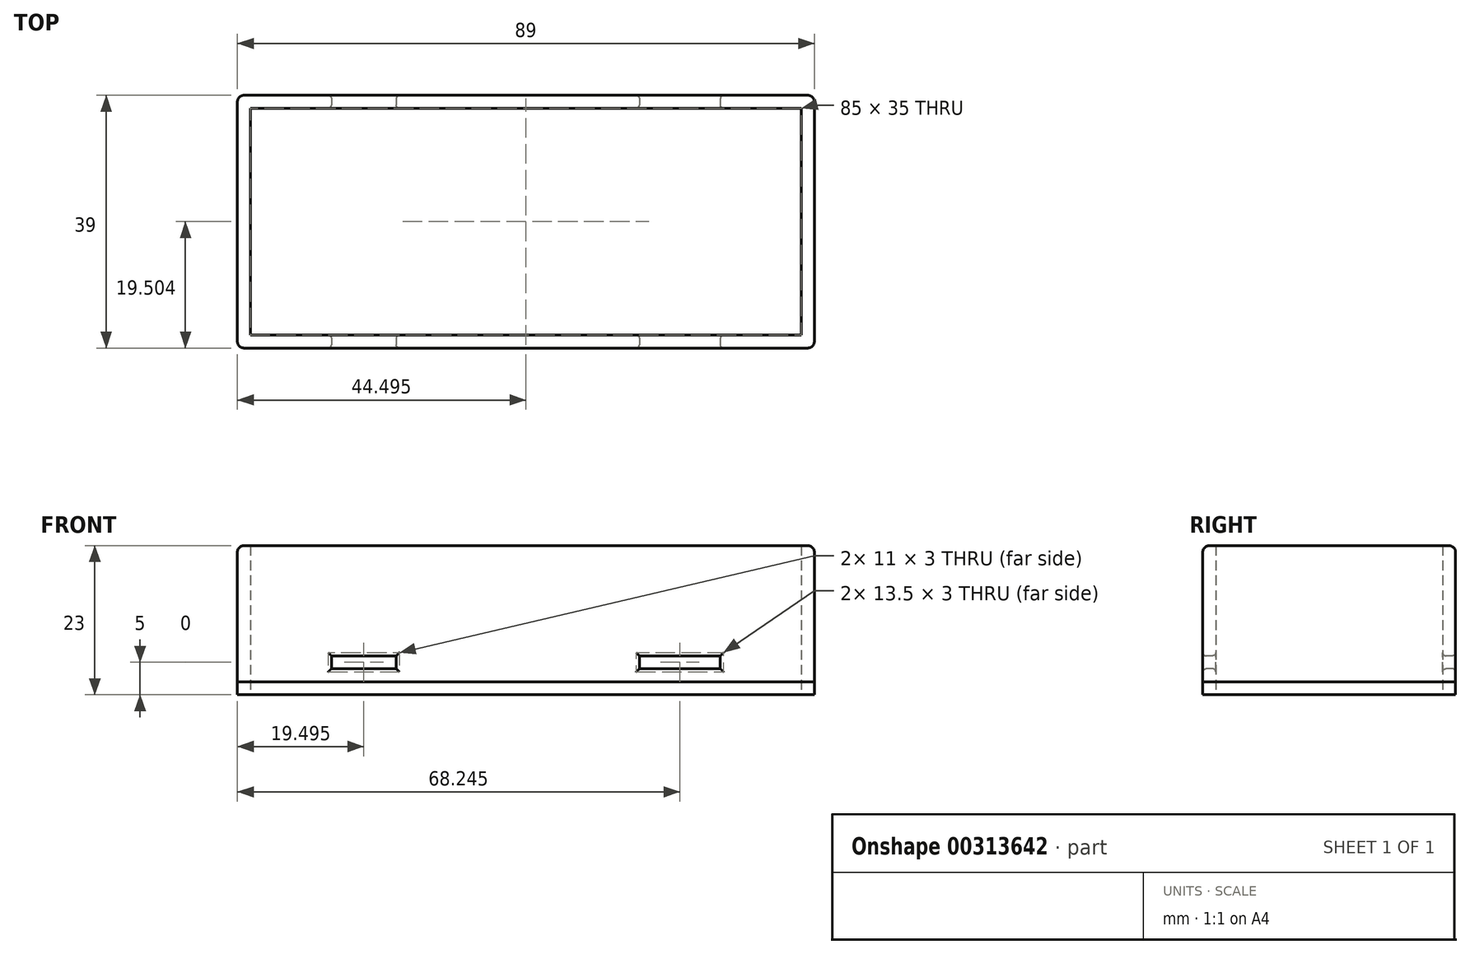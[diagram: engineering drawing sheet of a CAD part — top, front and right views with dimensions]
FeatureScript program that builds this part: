
annotation { "Feature Type Name" : "Feature", "Feature Type Description" : "" }
export const myFeature = defineFeature(function(context is Context, id is Id, definition is map)
    precondition{}
    {
        {
            var Q0;
            Q0=qCreatedBy(makeId("Top.planeOp"),FACE);
            var sketch = newSketch(context, id + "F0", { "sketchPlane" : qUnion([Q0])});
            skLineSegment(sketch, "E0.bottom", {"start": v(-28.21, 17.15) * mm, "end": v(60.79, 17.15) * mm});
            skLineSegment(sketch, "E0.top", {"start": v(-28.21, -21.85) * mm, "end": v(60.79, -21.85) * mm});
            skLineSegment(sketch, "E0.left", {"start": v(-28.21, 17.15) * mm, "end": v(-28.21, -21.85) * mm});
            skLineSegment(sketch, "E0.right", {"start": v(60.79, 17.15) * mm, "end": v(60.79, -21.85) * mm});
            skLineSegment(sketch, "E1.bottom", {"start": v(-26.21, 15.15) * mm, "end": v(58.79, 15.15) * mm});
            skLineSegment(sketch, "E1.top", {"start": v(-26.21, -19.85) * mm, "end": v(58.79, -19.85) * mm});
            skLineSegment(sketch, "E1.left", {"start": v(-26.21, 15.15) * mm, "end": v(-26.21, -19.85) * mm});
            skLineSegment(sketch, "E1.right", {"start": v(58.79, 15.15) * mm, "end": v(58.79, -19.85) * mm});
            skSolve(sketch);
        }
        {
            var Q0;
            Q0=makeQuery(id+"F0.imprint","IMPRINT",FACE,{"disambiguationData":[TD([[makeQuery(id+"F0.imprint","IMPRINT",EDGE,{"derivedFrom":sQuery(id+"F0.wireOp",EDGE,"E0.bottom")}),-1.0]])]});
            extrude(context, id + "F1", {"entities" : qUnion([Q0]), "depth" : 23 * mm});
        }
        {
            var Q0;
            Q0=qCreatedBy(makeId("Top.planeOp"),FACE);
            var sketch = newSketch(context, id + "F2", { "sketchPlane" : qUnion([Q0])});
            skLineSegment(sketch, "E2.bottom", {"start": v(-28.21, -21.85) * mm, "end": v(60.79, -21.85) * mm});
            skLineSegment(sketch, "E2.top", {"start": v(-28.21, 17.15) * mm, "end": v(60.79, 17.15) * mm});
            skLineSegment(sketch, "E2.left", {"start": v(-28.21, -21.85) * mm, "end": v(-28.21, 17.15) * mm});
            skLineSegment(sketch, "E2.right", {"start": v(60.79, -21.85) * mm, "end": v(60.79, 17.15) * mm});
            skSolve(sketch);
        }
        {
            var Q0;
            Q0 = qSketchRegion(id + "F2", true);
            extrude(context, id + "F3", {"entities" : qUnion([Q0]), "depth" : 2 * mm});
        }
        {
            var Q0;
            Q0=makeQuery(id+"F1.opExtrude","CAP_EDGE",EDGE,{"disambiguationData":[OSD([sQuery(id+"F0.wireOp",EDGE,"E0.bottom")])],"isStart":false});
            var Q1;
            Q1=makeQuery(id+"F1.opExtrude","CAP_EDGE",EDGE,{"disambiguationData":[OSD([sQuery(id+"F0.wireOp",EDGE,"E0.left")])],"isStart":false});
            var Q2;
            Q2=makeQuery(id+"F1.opExtrude","CAP_EDGE",EDGE,{"disambiguationData":[OSD([sQuery(id+"F0.wireOp",EDGE,"E0.top")])],"isStart":false});
            var Q3;
            Q3=makeQuery(id+"F1.opExtrude","CAP_EDGE",EDGE,{"disambiguationData":[OSD([sQuery(id+"F0.wireOp",EDGE,"E0.right")])],"isStart":false});
            var Q4;
            Q4=makeQuery(id+"F1.opExtrude","SWEPT_EDGE",EDGE,{"disambiguationData":[OSD([sQuery(id+"F0.wireOp",EDGE,"E0.bottom"),sQuery(id+"F0.wireOp",EDGE,"E0.right")])]});
            var Q5;
            Q5=makeQuery(id+"F1.opExtrude","SWEPT_EDGE",EDGE,{"disambiguationData":[OSD([sQuery(id+"F0.wireOp",EDGE,"E0.top"),sQuery(id+"F0.wireOp",EDGE,"E0.right")])]});
            var Q6;
            Q6=makeQuery(id+"F1.opExtrude","SWEPT_EDGE",EDGE,{"disambiguationData":[OSD([sQuery(id+"F0.wireOp",EDGE,"E0.bottom"),sQuery(id+"F0.wireOp",EDGE,"E0.left")])]});
            var Q7;
            Q7=makeQuery(id+"F1.opExtrude","SWEPT_EDGE",EDGE,{"disambiguationData":[OSD([sQuery(id+"F0.wireOp",EDGE,"E0.top"),sQuery(id+"F0.wireOp",EDGE,"E0.left")])]});
            fillet(context, id + "F4", {"entities" : qUnion([Q0, Q1, Q2, Q3, Q4, Q5, Q6, Q7]), "radius" : 1 * mm, "tangentPropagation" : true, "allowEdgeOverflow" : false});
        }
        {
            var Q0;
            Q0=makeQuery(id+"F3.opExtrude","SWEPT_EDGE",EDGE,{"disambiguationData":[OSD([sQuery(id+"F2.wireOp",EDGE,"E2.top"),sQuery(id+"F2.wireOp",EDGE,"E2.right")])]});
            var Q1;
            Q1=makeQuery(id+"F3.opExtrude","SWEPT_EDGE",EDGE,{"disambiguationData":[OSD([sQuery(id+"F2.wireOp",EDGE,"E2.top"),sQuery(id+"F2.wireOp",EDGE,"E2.left")])]});
            var Q2;
            Q2=makeQuery(id+"F3.opExtrude","SWEPT_EDGE",EDGE,{"disambiguationData":[OSD([sQuery(id+"F2.wireOp",EDGE,"E2.bottom"),sQuery(id+"F2.wireOp",EDGE,"E2.left")])]});
            var Q3;
            Q3=makeQuery(id+"F3.opExtrude","SWEPT_EDGE",EDGE,{"disambiguationData":[OSD([sQuery(id+"F2.wireOp",EDGE,"E2.bottom"),sQuery(id+"F2.wireOp",EDGE,"E2.right")])]});
            fillet(context, id + "F5", {"entities" : qUnion([Q0, Q1, Q2, Q3]), "radius" : 1 * mm, "tangentPropagation" : true, "allowEdgeOverflow" : false});
        }
        {
            var Q0;
            Q0=qCreatedBy(makeId("Front.planeOp"),FACE);
            var sketch = newSketch(context, id + "F6", { "sketchPlane" : qUnion([Q0])});
            skLineSegment(sketch, "E3.bottom", {"start": v(-13.71, 6) * mm, "end": v(-3.71, 6) * mm});
            skLineSegment(sketch, "E3.top", {"start": v(-13.71, 4) * mm, "end": v(-3.71, 4) * mm});
            skLineSegment(sketch, "E3.left", {"start": v(-13.71, 6) * mm, "end": v(-13.71, 4) * mm});
            skLineSegment(sketch, "E3.right", {"start": v(-3.71, 6) * mm, "end": v(-3.71, 4) * mm});
            skLineSegment(sketch, "E4.bottom", {"start": v(33.79, 6) * mm, "end": v(46.29, 6) * mm});
            skLineSegment(sketch, "E4.top", {"start": v(33.79, 4) * mm, "end": v(46.29, 4) * mm});
            skLineSegment(sketch, "E4.left", {"start": v(33.79, 6) * mm, "end": v(33.79, 4) * mm});
            skLineSegment(sketch, "E4.right", {"start": v(46.29, 6) * mm, "end": v(46.29, 4) * mm});
            skSolve(sketch);
        }
        {
            var Q0;
            Q0 = qSketchRegion(id + "F6", true);
            extrude(context, id + "F7", {"entities" : qUnion([Q0]), "operationType" : NewBodyOperationType.REMOVE, "endBound" : BoundingType.SYMMETRIC, "oppositeDirection" : true, "depth" : 100 * mm});
        }
        {
            var Q0;
            Q0=makeQuery(id+"F7.boolean.opBoolean","INTERSECT",EDGE,{"derivedFrom":[makeQuery(id+"F1.opExtrude","SWEPT_FACE",FACE,{"disambiguationData":[OSD([sQuery(id+"F0.wireOp",EDGE,"E0.top")])]}),makeQuery(id+"F7.opExtrude","SWEPT_FACE",FACE,{"disambiguationData":[OSD([sQuery(id+"F6.wireOp",EDGE,"E3.left")])]})]});
            var Q1;
            Q1=makeQuery(id+"F7.boolean.opBoolean","INTERSECT",EDGE,{"derivedFrom":[makeQuery(id+"F1.opExtrude","SWEPT_FACE",FACE,{"disambiguationData":[OSD([sQuery(id+"F0.wireOp",EDGE,"E0.top")])]}),makeQuery(id+"F7.opExtrude","SWEPT_FACE",FACE,{"disambiguationData":[OSD([sQuery(id+"F6.wireOp",EDGE,"E3.bottom")])]})]});
            var Q2;
            Q2=makeQuery(id+"F7.boolean.opBoolean","INTERSECT",EDGE,{"derivedFrom":[makeQuery(id+"F1.opExtrude","SWEPT_FACE",FACE,{"disambiguationData":[OSD([sQuery(id+"F0.wireOp",EDGE,"E0.top")])]}),makeQuery(id+"F7.opExtrude","SWEPT_FACE",FACE,{"disambiguationData":[OSD([sQuery(id+"F6.wireOp",EDGE,"E3.top")])]})]});
            var Q3;
            Q3=makeQuery(id+"F7.boolean.opBoolean","INTERSECT",EDGE,{"derivedFrom":[makeQuery(id+"F1.opExtrude","SWEPT_FACE",FACE,{"disambiguationData":[OSD([sQuery(id+"F0.wireOp",EDGE,"E0.top")])]}),makeQuery(id+"F7.opExtrude","SWEPT_FACE",FACE,{"disambiguationData":[OSD([sQuery(id+"F6.wireOp",EDGE,"E3.right")])]})]});
            var Q4;
            Q4=makeQuery(id+"F7.boolean.opBoolean","INTERSECT",EDGE,{"derivedFrom":[makeQuery(id+"F1.opExtrude","SWEPT_FACE",FACE,{"disambiguationData":[OSD([sQuery(id+"F0.wireOp",EDGE,"E0.top")])]}),makeQuery(id+"F7.opExtrude","SWEPT_FACE",FACE,{"disambiguationData":[OSD([sQuery(id+"F6.wireOp",EDGE,"E4.bottom")])]})]});
            var Q5;
            Q5=makeQuery(id+"F7.boolean.opBoolean","INTERSECT",EDGE,{"derivedFrom":[makeQuery(id+"F1.opExtrude","SWEPT_FACE",FACE,{"disambiguationData":[OSD([sQuery(id+"F0.wireOp",EDGE,"E0.top")])]}),makeQuery(id+"F7.opExtrude","SWEPT_FACE",FACE,{"disambiguationData":[OSD([sQuery(id+"F6.wireOp",EDGE,"E4.left")])]})]});
            var Q6;
            Q6=makeQuery(id+"F7.boolean.opBoolean","INTERSECT",EDGE,{"derivedFrom":[makeQuery(id+"F1.opExtrude","SWEPT_FACE",FACE,{"disambiguationData":[OSD([sQuery(id+"F0.wireOp",EDGE,"E0.top")])]}),makeQuery(id+"F7.opExtrude","SWEPT_FACE",FACE,{"disambiguationData":[OSD([sQuery(id+"F6.wireOp",EDGE,"E4.top")])]})]});
            var Q7;
            Q7=makeQuery(id+"F7.boolean.opBoolean","INTERSECT",EDGE,{"derivedFrom":[makeQuery(id+"F1.opExtrude","SWEPT_FACE",FACE,{"disambiguationData":[OSD([sQuery(id+"F0.wireOp",EDGE,"E0.top")])]}),makeQuery(id+"F7.opExtrude","SWEPT_FACE",FACE,{"disambiguationData":[OSD([sQuery(id+"F6.wireOp",EDGE,"E4.right")])]})]});
            var Q8;
            Q8=makeQuery(id+"F7.boolean.opBoolean","INTERSECT",EDGE,{"derivedFrom":[makeQuery(id+"F1.opExtrude","SWEPT_FACE",FACE,{"disambiguationData":[OSD([sQuery(id+"F0.wireOp",EDGE,"E1.bottom")])]}),makeQuery(id+"F7.opExtrude","SWEPT_FACE",FACE,{"disambiguationData":[OSD([sQuery(id+"F6.wireOp",EDGE,"E3.bottom")])]})]});
            var Q9;
            Q9=makeQuery(id+"F7.boolean.opBoolean","INTERSECT",EDGE,{"derivedFrom":[makeQuery(id+"F1.opExtrude","SWEPT_FACE",FACE,{"disambiguationData":[OSD([sQuery(id+"F0.wireOp",EDGE,"E1.bottom")])]}),makeQuery(id+"F7.opExtrude","SWEPT_FACE",FACE,{"disambiguationData":[OSD([sQuery(id+"F6.wireOp",EDGE,"E3.top")])]})]});
            var Q10;
            Q10=makeQuery(id+"F7.boolean.opBoolean","INTERSECT",EDGE,{"derivedFrom":[makeQuery(id+"F1.opExtrude","SWEPT_FACE",FACE,{"disambiguationData":[OSD([sQuery(id+"F0.wireOp",EDGE,"E1.bottom")])]}),makeQuery(id+"F7.opExtrude","SWEPT_FACE",FACE,{"disambiguationData":[OSD([sQuery(id+"F6.wireOp",EDGE,"E3.left")])]})]});
            var Q11;
            Q11=makeQuery(id+"F7.boolean.opBoolean","INTERSECT",EDGE,{"derivedFrom":[makeQuery(id+"F1.opExtrude","SWEPT_FACE",FACE,{"disambiguationData":[OSD([sQuery(id+"F0.wireOp",EDGE,"E1.bottom")])]}),makeQuery(id+"F7.opExtrude","SWEPT_FACE",FACE,{"disambiguationData":[OSD([sQuery(id+"F6.wireOp",EDGE,"E3.right")])]})]});
            var Q12;
            Q12=makeQuery(id+"F7.boolean.opBoolean","INTERSECT",EDGE,{"derivedFrom":[makeQuery(id+"F1.opExtrude","SWEPT_FACE",FACE,{"disambiguationData":[OSD([sQuery(id+"F0.wireOp",EDGE,"E1.bottom")])]}),makeQuery(id+"F7.opExtrude","SWEPT_FACE",FACE,{"disambiguationData":[OSD([sQuery(id+"F6.wireOp",EDGE,"E4.left")])]})]});
            var Q13;
            Q13=makeQuery(id+"F7.boolean.opBoolean","INTERSECT",EDGE,{"derivedFrom":[makeQuery(id+"F1.opExtrude","SWEPT_FACE",FACE,{"disambiguationData":[OSD([sQuery(id+"F0.wireOp",EDGE,"E1.bottom")])]}),makeQuery(id+"F7.opExtrude","SWEPT_FACE",FACE,{"disambiguationData":[OSD([sQuery(id+"F6.wireOp",EDGE,"E4.bottom")])]})]});
            var Q14;
            Q14=makeQuery(id+"F7.boolean.opBoolean","INTERSECT",EDGE,{"derivedFrom":[makeQuery(id+"F1.opExtrude","SWEPT_FACE",FACE,{"disambiguationData":[OSD([sQuery(id+"F0.wireOp",EDGE,"E1.bottom")])]}),makeQuery(id+"F7.opExtrude","SWEPT_FACE",FACE,{"disambiguationData":[OSD([sQuery(id+"F6.wireOp",EDGE,"E4.top")])]})]});
            var Q15;
            Q15=makeQuery(id+"F7.boolean.opBoolean","INTERSECT",EDGE,{"derivedFrom":[makeQuery(id+"F1.opExtrude","SWEPT_FACE",FACE,{"disambiguationData":[OSD([sQuery(id+"F0.wireOp",EDGE,"E1.bottom")])]}),makeQuery(id+"F7.opExtrude","SWEPT_FACE",FACE,{"disambiguationData":[OSD([sQuery(id+"F6.wireOp",EDGE,"E4.right")])]})]});
            var Q16;
            Q16=makeQuery(id+"F7.boolean.opBoolean","INTERSECT",EDGE,{"derivedFrom":[makeQuery(id+"F1.opExtrude","SWEPT_FACE",FACE,{"disambiguationData":[OSD([sQuery(id+"F0.wireOp",EDGE,"E0.bottom")])]}),makeQuery(id+"F7.opExtrude","SWEPT_FACE",FACE,{"disambiguationData":[OSD([sQuery(id+"F6.wireOp",EDGE,"E4.right")])]})]});
            var Q17;
            Q17=makeQuery(id+"F7.boolean.opBoolean","INTERSECT",EDGE,{"derivedFrom":[makeQuery(id+"F1.opExtrude","SWEPT_FACE",FACE,{"disambiguationData":[OSD([sQuery(id+"F0.wireOp",EDGE,"E0.bottom")])]}),makeQuery(id+"F7.opExtrude","SWEPT_FACE",FACE,{"disambiguationData":[OSD([sQuery(id+"F6.wireOp",EDGE,"E4.bottom")])]})]});
            var Q18;
            Q18=makeQuery(id+"F7.boolean.opBoolean","INTERSECT",EDGE,{"derivedFrom":[makeQuery(id+"F1.opExtrude","SWEPT_FACE",FACE,{"disambiguationData":[OSD([sQuery(id+"F0.wireOp",EDGE,"E0.bottom")])]}),makeQuery(id+"F7.opExtrude","SWEPT_FACE",FACE,{"disambiguationData":[OSD([sQuery(id+"F6.wireOp",EDGE,"E4.left")])]})]});
            var Q19;
            Q19=makeQuery(id+"F7.boolean.opBoolean","INTERSECT",EDGE,{"derivedFrom":[makeQuery(id+"F1.opExtrude","SWEPT_FACE",FACE,{"disambiguationData":[OSD([sQuery(id+"F0.wireOp",EDGE,"E0.bottom")])]}),makeQuery(id+"F7.opExtrude","SWEPT_FACE",FACE,{"disambiguationData":[OSD([sQuery(id+"F6.wireOp",EDGE,"E4.top")])]})]});
            var Q20;
            Q20=makeQuery(id+"F7.boolean.opBoolean","INTERSECT",EDGE,{"derivedFrom":[makeQuery(id+"F1.opExtrude","SWEPT_FACE",FACE,{"disambiguationData":[OSD([sQuery(id+"F0.wireOp",EDGE,"E0.bottom")])]}),makeQuery(id+"F7.opExtrude","SWEPT_FACE",FACE,{"disambiguationData":[OSD([sQuery(id+"F6.wireOp",EDGE,"E3.left")])]})]});
            var Q21;
            Q21=makeQuery(id+"F7.boolean.opBoolean","INTERSECT",EDGE,{"derivedFrom":[makeQuery(id+"F1.opExtrude","SWEPT_FACE",FACE,{"disambiguationData":[OSD([sQuery(id+"F0.wireOp",EDGE,"E0.bottom")])]}),makeQuery(id+"F7.opExtrude","SWEPT_FACE",FACE,{"disambiguationData":[OSD([sQuery(id+"F6.wireOp",EDGE,"E3.top")])]})]});
            var Q22;
            Q22=makeQuery(id+"F7.boolean.opBoolean","INTERSECT",EDGE,{"derivedFrom":[makeQuery(id+"F1.opExtrude","SWEPT_FACE",FACE,{"disambiguationData":[OSD([sQuery(id+"F0.wireOp",EDGE,"E0.bottom")])]}),makeQuery(id+"F7.opExtrude","SWEPT_FACE",FACE,{"disambiguationData":[OSD([sQuery(id+"F6.wireOp",EDGE,"E3.right")])]})]});
            var Q23;
            Q23=makeQuery(id+"F7.boolean.opBoolean","INTERSECT",EDGE,{"derivedFrom":[makeQuery(id+"F1.opExtrude","SWEPT_FACE",FACE,{"disambiguationData":[OSD([sQuery(id+"F0.wireOp",EDGE,"E0.bottom")])]}),makeQuery(id+"F7.opExtrude","SWEPT_FACE",FACE,{"disambiguationData":[OSD([sQuery(id+"F6.wireOp",EDGE,"E3.bottom")])]})]});
            var Q24;
            Q24=makeQuery(id+"F7.boolean.opBoolean","INTERSECT",EDGE,{"derivedFrom":[makeQuery(id+"F1.opExtrude","SWEPT_FACE",FACE,{"disambiguationData":[OSD([sQuery(id+"F0.wireOp",EDGE,"E1.top")])]}),makeQuery(id+"F7.opExtrude","SWEPT_FACE",FACE,{"disambiguationData":[OSD([sQuery(id+"F6.wireOp",EDGE,"E3.right")])]})]});
            var Q25;
            Q25=makeQuery(id+"F7.boolean.opBoolean","INTERSECT",EDGE,{"derivedFrom":[makeQuery(id+"F1.opExtrude","SWEPT_FACE",FACE,{"disambiguationData":[OSD([sQuery(id+"F0.wireOp",EDGE,"E1.top")])]}),makeQuery(id+"F7.opExtrude","SWEPT_FACE",FACE,{"disambiguationData":[OSD([sQuery(id+"F6.wireOp",EDGE,"E3.top")])]})]});
            var Q26;
            Q26=makeQuery(id+"F7.boolean.opBoolean","INTERSECT",EDGE,{"derivedFrom":[makeQuery(id+"F1.opExtrude","SWEPT_FACE",FACE,{"disambiguationData":[OSD([sQuery(id+"F0.wireOp",EDGE,"E1.top")])]}),makeQuery(id+"F7.opExtrude","SWEPT_FACE",FACE,{"disambiguationData":[OSD([sQuery(id+"F6.wireOp",EDGE,"E3.left")])]})]});
            var Q27;
            Q27=makeQuery(id+"F7.boolean.opBoolean","INTERSECT",EDGE,{"derivedFrom":[makeQuery(id+"F1.opExtrude","SWEPT_FACE",FACE,{"disambiguationData":[OSD([sQuery(id+"F0.wireOp",EDGE,"E1.top")])]}),makeQuery(id+"F7.opExtrude","SWEPT_FACE",FACE,{"disambiguationData":[OSD([sQuery(id+"F6.wireOp",EDGE,"E3.bottom")])]})]});
            var Q28;
            Q28=makeQuery(id+"F7.boolean.opBoolean","INTERSECT",EDGE,{"derivedFrom":[makeQuery(id+"F1.opExtrude","SWEPT_FACE",FACE,{"disambiguationData":[OSD([sQuery(id+"F0.wireOp",EDGE,"E1.top")])]}),makeQuery(id+"F7.opExtrude","SWEPT_FACE",FACE,{"disambiguationData":[OSD([sQuery(id+"F6.wireOp",EDGE,"E4.right")])]})]});
            var Q29;
            Q29=makeQuery(id+"F7.boolean.opBoolean","INTERSECT",EDGE,{"derivedFrom":[makeQuery(id+"F1.opExtrude","SWEPT_FACE",FACE,{"disambiguationData":[OSD([sQuery(id+"F0.wireOp",EDGE,"E1.top")])]}),makeQuery(id+"F7.opExtrude","SWEPT_FACE",FACE,{"disambiguationData":[OSD([sQuery(id+"F6.wireOp",EDGE,"E4.top")])]})]});
            var Q30;
            Q30=makeQuery(id+"F7.boolean.opBoolean","INTERSECT",EDGE,{"derivedFrom":[makeQuery(id+"F1.opExtrude","SWEPT_FACE",FACE,{"disambiguationData":[OSD([sQuery(id+"F0.wireOp",EDGE,"E1.top")])]}),makeQuery(id+"F7.opExtrude","SWEPT_FACE",FACE,{"disambiguationData":[OSD([sQuery(id+"F6.wireOp",EDGE,"E4.left")])]})]});
            var Q31;
            Q31=makeQuery(id+"F7.boolean.opBoolean","INTERSECT",EDGE,{"derivedFrom":[makeQuery(id+"F1.opExtrude","SWEPT_FACE",FACE,{"disambiguationData":[OSD([sQuery(id+"F0.wireOp",EDGE,"E1.top")])]}),makeQuery(id+"F7.opExtrude","SWEPT_FACE",FACE,{"disambiguationData":[OSD([sQuery(id+"F6.wireOp",EDGE,"E4.bottom")])]})]});
            fillet(context, id + "F8", {"entities" : qUnion([Q0, Q1, Q2, Q3, Q4, Q5, Q6, Q7, Q8, Q9, Q10, Q11, Q12, Q13, Q14, Q15, Q16, Q17, Q18, Q19, Q20, Q21, Q22, Q23, Q24, Q25, Q26, Q27, Q28, Q29, Q30, Q31]), "radius" : 0.5 * mm, "tangentPropagation" : true, "allowEdgeOverflow" : false});
        }
    });
